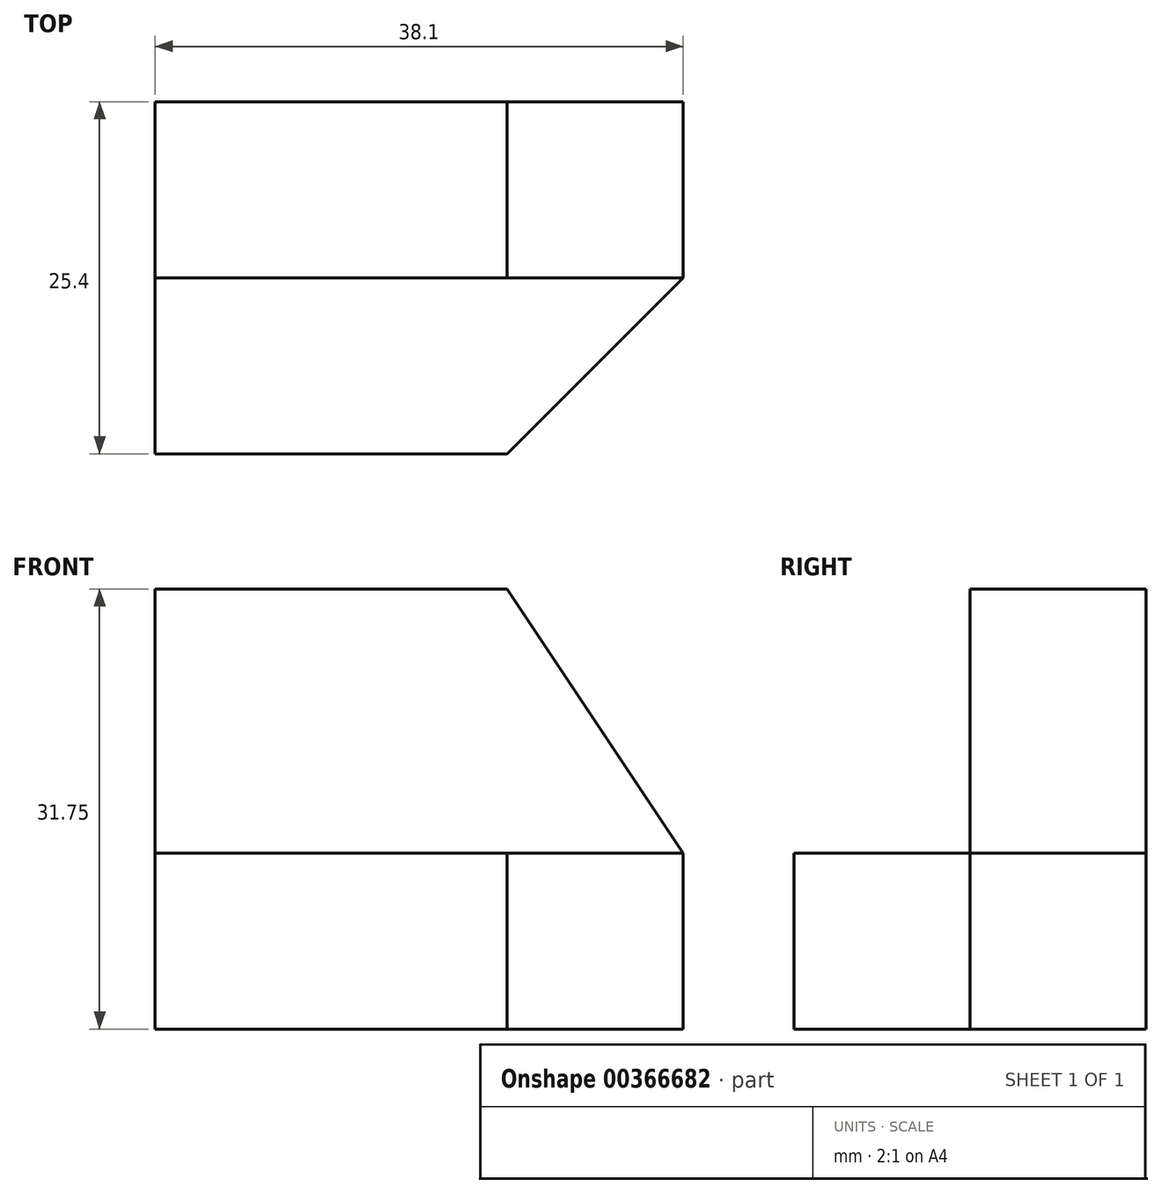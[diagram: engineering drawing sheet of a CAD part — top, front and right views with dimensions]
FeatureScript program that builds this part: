
annotation { "Feature Type Name" : "Feature", "Feature Type Description" : "" }
export const myFeature = defineFeature(function(context is Context, id is Id, definition is map)
    precondition{}
    {
        {
            var Q0;
            Q0=qCreatedBy(makeId("Front.planeOp"),FACE);
            var sketch = newSketch(context, id + "F0", { "sketchPlane" : qUnion([Q0])});
            skLineSegment(sketch, "E0", {"start": v(-56.52, 0) * mm, "end": v(-56.52, 31.75) * mm});
            skLineSegment(sketch, "E1", {"start": v(-56.52, 31.75) * mm, "end": v(-18.42, 31.75) * mm});
            skLineSegment(sketch, "E2", {"start": v(-18.42, 31.75) * mm, "end": v(-18.42, 0) * mm});
            skLineSegment(sketch, "E3", {"start": v(-18.42, 0) * mm, "end": v(-56.52, 0) * mm});
            skSolve(sketch);
        }
        {
            var Q0;
            Q0=makeQuery(id+"F0.imprint","IMPRINT",FACE,{"disambiguationData":[TD([[makeQuery(id+"F0.imprint","IMPRINT",EDGE,{"derivedFrom":sQuery(id+"F0.wireOp",EDGE,"E0")}),-1.0]])]});
            extrude(context, id + "F1", {"entities" : qUnion([Q0]), "depth" : 25.4 * mm});
        }
        {
            var Q0;
            Q0=makeQuery(id+"F1.opExtrude","SWEPT_FACE",FACE,{"disambiguationData":[OSD([sQuery(id+"F0.wireOp",EDGE,"E2")])]});
            var sketch = newSketch(context, id + "F2", { "sketchPlane" : qUnion([Q0])});
            skLineSegment(sketch, "E4", {"start": v(-25.4, 12.7) * mm, "end": v(-12.7, 12.7) * mm});
            skLineSegment(sketch, "E5", {"start": v(-12.7, 12.7) * mm, "end": v(-12.7, 31.75) * mm});
            skSolve(sketch);
        }
        {
            var Q0;
            {var subQ0=sQuery(id+"F2.wireOp",EDGE,"E4");Q0=makeQuery(id+"F2.imprint","IMPRINT",FACE,{"disambiguationData":[TD([[makeQuery(id+"F2.imprint","IMPRINT",EDGE,{"derivedFrom":subQ0}),1.0]])]});}
            extrude(context, id + "F3", {"entities" : qUnion([Q0]), "operationType" : NewBodyOperationType.REMOVE, "oppositeDirection" : true, "depth" : 38.1 * mm});
        }
        {
            var Q0;
            Q0=makeQuery(id+"F3.boolean.opBoolean","COPY",FACE,{"derivedFrom":makeQuery(id+"F3.opExtrude","SWEPT_FACE",FACE,{"disambiguationData":[OSD([sQuery(id+"F2.wireOp",EDGE,"E4")])]})});
            var sketch = newSketch(context, id + "F4", { "sketchPlane" : qUnion([Q0])});
            skLineSegment(sketch, "E6", {"start": v(-18.42, -12.7) * mm, "end": v(-31.12, -25.4) * mm});
            skSolve(sketch);
        }
        {
            var Q0;
            {var subQ0=sQuery(id+"F4.wireOp",EDGE,"E6");Q0=makeQuery(id+"F4.imprint","IMPRINT",FACE,{"disambiguationData":[TD([[makeQuery(id+"F4.imprint","IMPRINT",EDGE,{"derivedFrom":subQ0}),1.0]])]});}
            extrude(context, id + "F5", {"entities" : qUnion([Q0]), "operationType" : NewBodyOperationType.REMOVE, "oppositeDirection" : true, "depth" : 25.4 * mm});
        }
        {
            var Q0;
            Q0=makeQuery(id+"F3.boolean.opBoolean","COPY",FACE,{"derivedFrom":makeQuery(id+"F3.opExtrude","SWEPT_FACE",FACE,{"disambiguationData":[OSD([sQuery(id+"F2.wireOp",EDGE,"E5")])]})});
            var sketch = newSketch(context, id + "F6", { "sketchPlane" : qUnion([Q0])});
            skLineSegment(sketch, "E7", {"start": v(-31.12, 31.75) * mm, "end": v(-18.42, 12.7) * mm});
            skSolve(sketch);
        }
        {
            var Q0;
            {var subQ0=sQuery(id+"F6.wireOp",EDGE,"E7");Q0=makeQuery(id+"F6.imprint","IMPRINT",FACE,{"disambiguationData":[TD([[makeQuery(id+"F6.imprint","IMPRINT",EDGE,{"derivedFrom":subQ0}),1.0]])]});}
            extrude(context, id + "F7", {"entities" : qUnion([Q0]), "operationType" : NewBodyOperationType.REMOVE, "oppositeDirection" : true, "depth" : 25.4 * mm});
        }
    });
